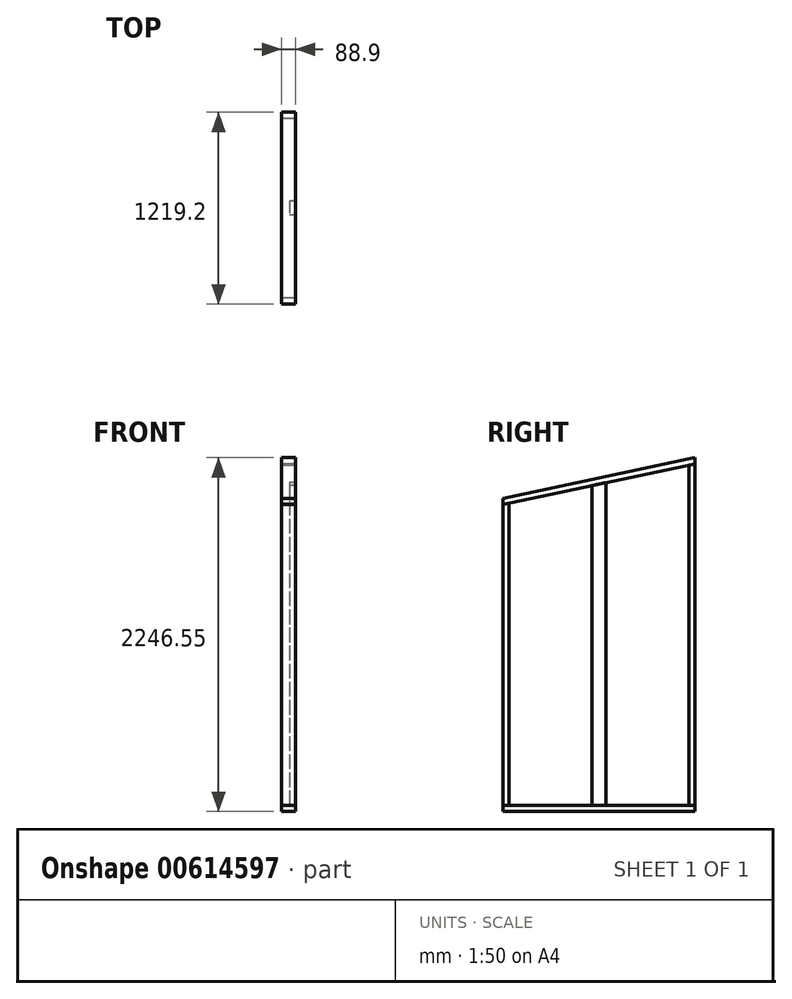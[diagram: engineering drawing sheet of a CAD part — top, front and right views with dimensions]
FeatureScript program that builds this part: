
annotation { "Feature Type Name" : "Feature", "Feature Type Description" : "" }
export const myFeature = defineFeature(function(context is Context, id is Id, definition is map)
    precondition{}
    {
        {
            var Q0;
            Q0=qCreatedBy(makeId("Right.planeOp"),FACE);
            var sketch = newSketch(context, id + "F0", { "sketchPlane" : qUnion([Q0])});
            skLineSegment(sketch, "E0", {"start": v(0, 0) * mm, "end": v(0, 1968.5) * mm});
            skLineSegment(sketch, "E1", {"start": v(0, 1968.5) * mm, "end": v(1397, 2265.44) * mm});
            skLineSegment(sketch, "E2", {"start": v(1397, 2265.44) * mm, "end": v(1397, 0) * mm});
            skLineSegment(sketch, "E3", {"start": v(1397, 0) * mm, "end": v(0, 0) * mm});
            skLineSegment(sketch, "E4", {"start": v(88.9, 0) * mm, "end": v(88.9, 1987.4) * mm});
            skLineSegment(sketch, "E5", {"start": v(1308.1, 0) * mm, "end": v(1308.1, 2246.55) * mm});
            skCircle(sketch, "E6", {"center": v(876.3, 1753.54) * mm, "radius": 381 * mm});
            skLineSegment(sketch, "E7", {"start": v(876.3, 2134.54) * mm, "end": v(876.3, 1372.54) * mm});
            skSolve(sketch);
        }
        {
            var Q0;
            Q0=qCreatedBy(makeId("Top.planeOp"),FACE);
            var sketch = newSketch(context, id + "F1", { "sketchPlane" : qUnion([Q0])});
            skLineSegment(sketch, "E8.bottom", {"start": v(0, 1308.1) * mm, "end": v(88.9, 1308.1) * mm});
            skLineSegment(sketch, "E8.top", {"start": v(0, 88.9) * mm, "end": v(88.9, 88.9) * mm});
            skLineSegment(sketch, "E8.left", {"start": v(0, 1308.1) * mm, "end": v(0, 88.9) * mm});
            skLineSegment(sketch, "E8.right", {"start": v(88.9, 1308.1) * mm, "end": v(88.9, 88.9) * mm});
            skSolve(sketch);
        }
        {
            var Q0;
            Q0 = qSketchRegion(id + "F1", true);
            extrude(context, id + "F2", {"entities" : qUnion([Q0]), "depth" : 38.1 * mm, "offsetDistance" : 25.4 * mm});
        }
        {
            var Q0;
            Q0=makeQuery(id+"F2.opExtrude","CAP_FACE",FACE,{"disambiguationData":[OSD([sQuery(id+"F1.wireOp",EDGE,"E8.bottom"),sQuery(id+"F1.wireOp",EDGE,"E8.top"),sQuery(id+"F1.wireOp",EDGE,"E8.left"),sQuery(id+"F1.wireOp",EDGE,"E8.right")])],"isStart":false});
            var sketch = newSketch(context, id + "F3", { "sketchPlane" : qUnion([Q0])});
            skLineSegment(sketch, "E9.bottom", {"start": v(88.9, 127) * mm, "end": v(0, 127) * mm});
            skLineSegment(sketch, "E9.top", {"start": v(88.9, 88.9) * mm, "end": v(0, 88.9) * mm});
            skLineSegment(sketch, "E9.left", {"start": v(88.9, 127) * mm, "end": v(88.9, 88.9) * mm});
            skLineSegment(sketch, "E9.right", {"start": v(0, 127) * mm, "end": v(0, 88.9) * mm});
            skLineSegment(sketch, "E10.bottom", {"start": v(0, 1308.1) * mm, "end": v(88.9, 1308.1) * mm});
            skLineSegment(sketch, "E10.top", {"start": v(0, 1270) * mm, "end": v(88.9, 1270) * mm});
            skLineSegment(sketch, "E10.left", {"start": v(0, 1308.1) * mm, "end": v(0, 1270) * mm});
            skLineSegment(sketch, "E10.right", {"start": v(88.9, 1308.1) * mm, "end": v(88.9, 1270) * mm});
            skLineSegment(sketch, "E11", {"start": v(0, 698.5) * mm, "end": v(88.9, 698.5) * mm, "construction": true});
            skLineSegment(sketch, "E12.bottom", {"start": v(88.9, 742.95) * mm, "end": v(50.8, 742.95) * mm});
            skLineSegment(sketch, "E12.top", {"start": v(88.9, 654.05) * mm, "end": v(50.8, 654.05) * mm});
            skLineSegment(sketch, "E12.left", {"start": v(88.9, 742.95) * mm, "end": v(88.9, 654.05) * mm});
            skLineSegment(sketch, "E12.right", {"start": v(50.8, 742.95) * mm, "end": v(50.8, 654.05) * mm});
            skSolve(sketch);
        }
        {
            var Q0;
            Q0 = qSketchRegion(id + "F3", true);
            extrude(context, id + "F4", {"entities" : qUnion([Q0]), "depth" : 2540 * mm, "offsetDistance" : 25.4 * mm});
        }
        {
            var Q0;
            Q0=qCreatedBy(makeId("Right.planeOp"),FACE);
            var sketch = newSketch(context, id + "F5", { "sketchPlane" : qUnion([Q0])});
            skLineSegment(sketch, "E13", {"start": v(88.9, 2578.1) * mm, "end": v(88.9, 1948.45) * mm});
            skLineSegment(sketch, "E14", {"start": v(88.9, 1948.45) * mm, "end": v(1308.1, 2207.6) * mm});
            skLineSegment(sketch, "E15", {"start": v(1308.1, 2207.6) * mm, "end": v(1308.1, 2578.1) * mm});
            skLineSegment(sketch, "E16", {"start": v(1308.1, 2578.1) * mm, "end": v(88.9, 2578.1) * mm});
            skSolve(sketch);
        }
        {
            var Q0;
            Q0 = qSketchRegion(id + "F5", true);
            extrude(context, id + "F6", {"entities" : qUnion([Q0]), "operationType" : NewBodyOperationType.REMOVE, "endBound" : BoundingType.THROUGH_ALL, "depth" : 25.4 * mm, "offsetDistance" : 25.4 * mm});
        }
        {
            var Q0;
            Q0=qCreatedBy(makeId("Right.planeOp"),FACE);
            var sketch = newSketch(context, id + "F7", { "sketchPlane" : qUnion([Q0])});
            skLineSegment(sketch, "E17", {"start": v(88.9, 1948.45) * mm, "end": v(1308.1, 2207.6) * mm});
            skLineSegment(sketch, "E18", {"start": v(1308.1, 2207.6) * mm, "end": v(1308.1, 2246.55) * mm});
            skLineSegment(sketch, "E19", {"start": v(1308.1, 2246.55) * mm, "end": v(88.9, 1987.4) * mm});
            skLineSegment(sketch, "E20", {"start": v(88.9, 1987.4) * mm, "end": v(88.9, 1948.45) * mm});
            skSolve(sketch);
        }
        {
            var Q0;
            Q0 = qSketchRegion(id + "F7", true);
            extrude(context, id + "F8", {"entities" : qUnion([Q0]), "depth" : 88.9 * mm, "offsetDistance" : 25.4 * mm});
        }
    });
